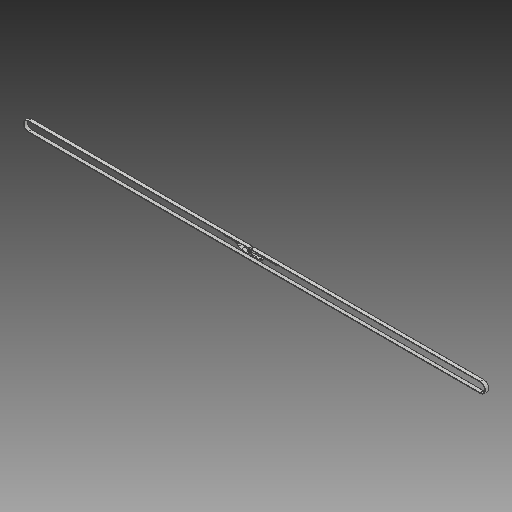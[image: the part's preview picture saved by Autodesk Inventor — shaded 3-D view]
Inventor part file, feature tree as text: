
AUTODESK INVENTOR PART (.ipt)
format: ipt  version: 2018 (Build 220112000, 112)  size: 164,864 bytes
history: native  units: mm
features: extrude x1, sketch x1
ambient origin geometry x8: Origin, YZ Plane, XZ Plane, XY Plane, X Axis, Y Axis, Z Axis, Center Point
bodies: Solid1 (feature_tree)
feature tree (2):
  extrude  "Extrusion1"  Depth=1.0mm
  sketch  "Sketch1"  dims[d0=1.0mm d1=1.0mm d2=5.0mm d3=0.0mm]
